# Revit family: 18552-presto
name_source: partatom
category: Plumbing Fixtures
units: mm (PartAtom-declared; Revit-internal decimal feet)

## family parameters
Always vertical = Yes
Cut with Voids When Loaded = No
Maintain Annotation Orientation = No
OmniClass Number = 23.45.00.00
OmniClass Title = Sanitary, Laundry, and Cleaning Equipment
Part Type = Normal
Room Calculation Point = No
Round Connector Dimension = Use Diameter
Shared = No
Work Plane-Based = No

## types (1)
- 18552- presto
    -Delivered with = 1 PVC angle tube Ø 32 mm and 1 junction nozzle male 50mm
    > Standards & approvals = 00-hour neutral salt spray resistant (NSS) in accordance with ISO 9227
    Default Elevation = 0 mm  [stored 0 ft]
    Description = Self-supporting mounting frame to use with P1000XL 14250, 14251, 14300, 14303, 14301, 55434, 55432, 55476, 55478
    Model = 18552
    Recommended pressure = 3.0 bar
    URL = https://www.prestodatashare.com
    brand = LES ROBINETS PRESTO
    flow = 6.0 L/s
    flow time = 1.0 s
    min flow = 1.0 L/s
    min pressure = 1.0 bar
    power = 0 W
    pressure = 5.0 bar
    range = Self-supporting mounting frame
    ref = 18552 - Self-supporting mounting frame for PRESTO 1000 XL

note: [stored X ft] marks values corroborated as IEEE doubles in the binary element streams (Revit-internal decimal feet)

## geometry (parser evidence)
native form markers: Sweep x2
no freeform markers — native parametric forms only
